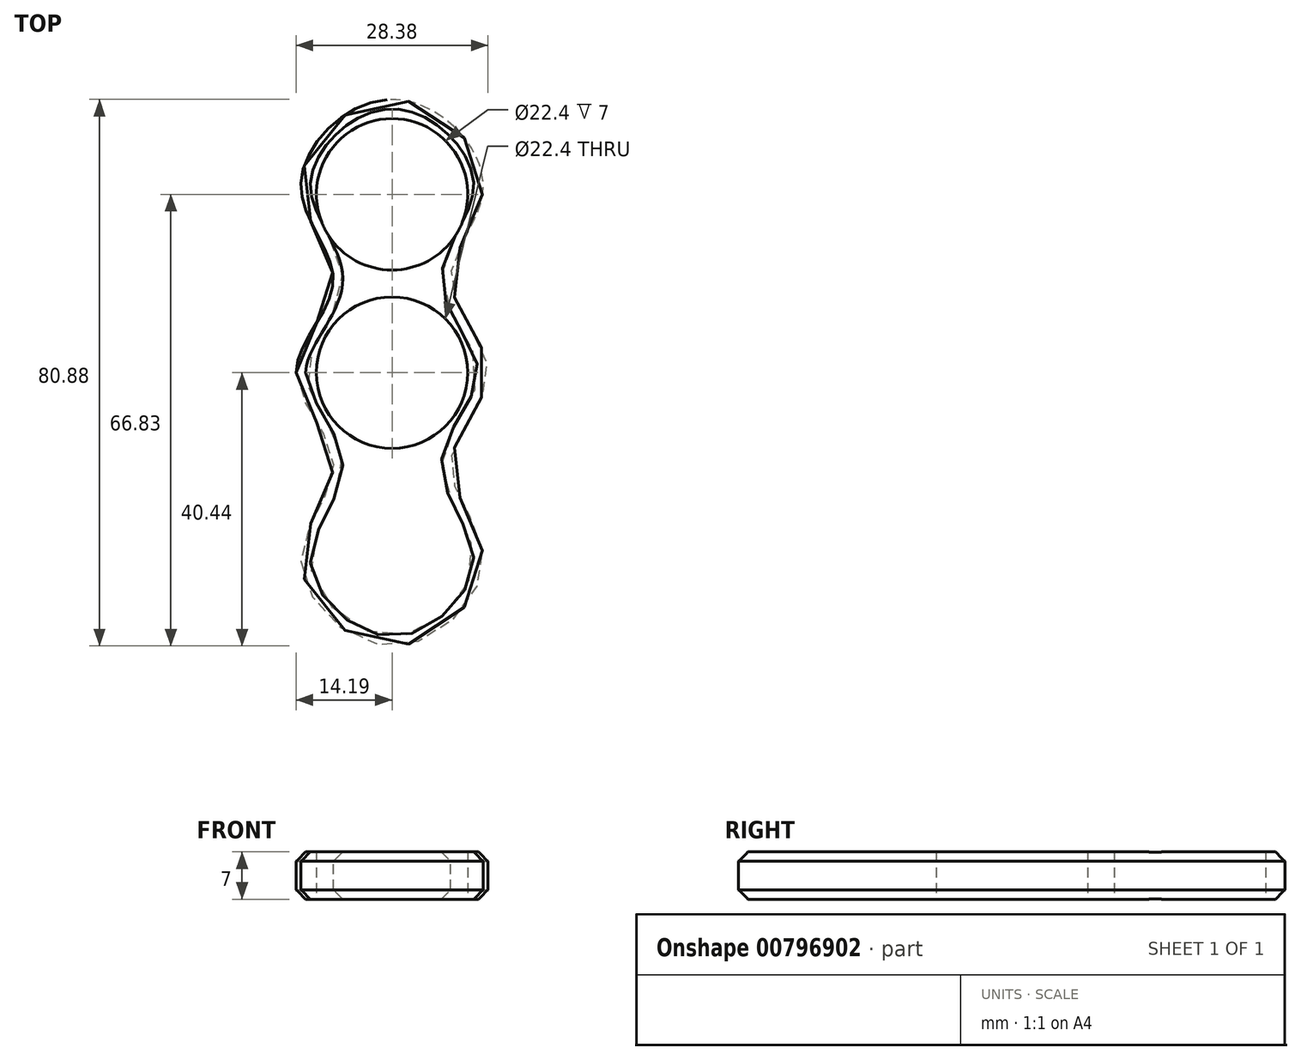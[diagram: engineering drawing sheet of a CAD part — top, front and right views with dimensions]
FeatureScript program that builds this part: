
annotation { "Feature Type Name" : "Feature", "Feature Type Description" : "" }
export const myFeature = defineFeature(function(context is Context, id is Id, definition is map)
    precondition{}
    {
        {
            var Q0;
            Q0=qCreatedBy(makeId("Top.planeOp"),FACE);
            var sketch = newSketch(context, id + "F0", { "sketchPlane" : qUnion([Q0])});
            skCircle(sketch, "E0", {"center": v(0, 0) * mm, "radius": 11.2 * mm});
            skCircle(sketch, "E1", {"center": v(0, 26.4) * mm, "radius": 11.2 * mm});
            skCircle(sketch, "E2.MirrorC", {"center": v(0, -26.4) * mm, "radius": 11.2 * mm});
            skSolve(sketch);
        }
        {
            var Q0;
            Q0=qCreatedBy(makeId("Top.planeOp"),FACE);
            var sketch = newSketch(context, id + "F1", { "sketchPlane" : qUnion([Q0])});
            skPoint(sketch, "E3", {"position": v(-14.2, 0) * mm});
            skPoint(sketch, "E4", {"position": v(0, 40.44) * mm});
            skPoint(sketch, "E5", {"position": v(13.5, 28.02) * mm});
            skPoint(sketch, "E6.MirrorP", {"position": v(-13.5, 28.02) * mm});
            skPoint(sketch, "E7.MirrorP", {"position": v(14.2, 0) * mm});
            skPoint(sketch, "E8.MirrorP", {"position": v(-13.5, -28.02) * mm});
            skPoint(sketch, "E9.MirrorP", {"position": v(13.5, -28.02) * mm});
            skPoint(sketch, "E10.MirrorP", {"position": v(0, -40.44) * mm});
            skPoint(sketch, "E11", {"position": v(-8.7, 13.53) * mm});
            skPoint(sketch, "E12.MirrorP", {"position": v(8.7, 13.53) * mm});
            skPoint(sketch, "E13.MirrorP", {"position": v(8.7, -13.53) * mm});
            skPoint(sketch, "E14.MirrorP", {"position": v(-8.7, -13.53) * mm});
            skFitSpline(sketch, "E15", {"points": [v(-14.2, 0) * mm, v(-8.7, 13.53) * mm, v(-13.5, 28.02) * mm, v(0, 40.44) * mm, v(13.5, 28.02) * mm, v(8.7, 13.53) * mm, v(14.2, 0) * mm, v(8.7, -13.53) * mm, v(13.5, -28.02) * mm, v(0, -40.44) * mm, v(-13.5, -28.02) * mm, v(-8.7, -13.53) * mm, v(-14.2, 0) * mm]});
            skSolve(sketch);
        }
        {
            var Q0;
            Q0=makeQuery(id+"F1.imprint","IMPRINT",FACE,{"disambiguationData":[TD([[makeQuery(id+"F1.imprint","IMPRINT",EDGE,{"derivedFrom":sQuery(id+"F1.wireOp",EDGE,"E15")}),-1.0]])]});
            extrude(context, id + "F2", {"entities" : qUnion([Q0]), "depth" : 7 * mm, "offsetDistance" : 25.4 * mm});
        }
        {
            var Q0;
            Q0=makeQuery(id+"F0.imprint","IMPRINT",FACE,{"disambiguationData":[TD([[makeQuery(id+"F0.imprint","IMPRINT",EDGE,{"derivedFrom":sQuery(id+"F0.wireOp",EDGE,"E0")}),1.0]])]});
            var Q1;
            Q1=makeQuery(id+"F0.imprint","IMPRINT",FACE,{"disambiguationData":[TD([[makeQuery(id+"F0.imprint","IMPRINT",EDGE,{"derivedFrom":sQuery(id+"F0.wireOp",EDGE,"E2.MirrorC")}),-1.0]])]});
            var Q2;
            Q2=makeQuery(id+"F0.imprint","IMPRINT",FACE,{"disambiguationData":[TD([[makeQuery(id+"F0.imprint","IMPRINT",EDGE,{"derivedFrom":sQuery(id+"F0.wireOp",EDGE,"E1")}),1.0]])]});
            extrude(context, id + "F3", {"entities" : qUnion([Q0, Q1, Q2]), "operationType" : NewBodyOperationType.REMOVE, "endBound" : BoundingType.THROUGH_ALL, "depth" : 25.4 * mm, "offsetDistance" : 25.4 * mm});
        }
        {
            var Q0;
            Q0=makeQuery(id+"F2.opExtrude","CAP_EDGE",EDGE,{"disambiguationData":[OSD([sQuery(id+"F1.wireOp",EDGE,"E15")])],"isStart":false});
            var Q1;
            Q1=makeQuery(id+"F2.opExtrude","CAP_EDGE",EDGE,{"disambiguationData":[OSD([sQuery(id+"F1.wireOp",EDGE,"E15")])],"isStart":true});
            chamfer(context, id + "F4", {"entities" : qUnion([Q0, Q1]), "width" : 1.4 * mm, "tangentPropagation" : true});
        }
    });
